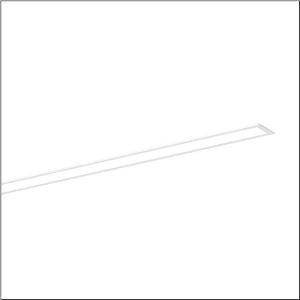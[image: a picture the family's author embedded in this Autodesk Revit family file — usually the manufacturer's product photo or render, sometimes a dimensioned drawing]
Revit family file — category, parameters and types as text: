
# Revit family: silica_r__21_51mx10db42wb_30ee
name_source: partatom
category: Lighting Fixtures
units: mm (PartAtom-declared; Revit-internal decimal feet)

## family parameters
Cut with Voids When Loaded = No
Host = Face
Light Source = No
Part Type = Normal
Room Calculation Point = No
Round Connector Dimension = Use Diameter
Shared = No

## types (1)
- --- (1 x LED, 3000 lm, 19 W, 4000K)
    Apparent Load = 19 VA
    CIE Flux Codes = 48 79 96 100 100
    Color Rendering = 80
    Color Temperature = 4000K
    Default Elevation = 1800 mm
    Description = Silica® 21, office luminaire, primary optical cover: cover, of PMMA, opal, light emission: direct distribution, primary light characteristic: symmetric, installation type: recessed, LED, rated luminous flux: 3.000lm, luminous efficacy: 158lm/W, light colour: 840, colour temperature: 4000K, with terminal, 3+2-pole, max. 2.5mm², mains connection: 220..240V, AC, 50/60Hz, rated input power: 19W, luminaire housing, of aluminium, traffic white (RAL 9016), length: 1.528mm, width: 79mm, height: 53mm, protection rating (complete): IP20, insulation class (complete): insulation class I (protective earthing), certification: CE, permissible operating ambient temperature: 0..+35°C, standard: EN 50419, packaging unit: 1 piece
    Height = 0 mm  [stored 0 ft]
    Lamp = 1 x LED
    Lamp Light Flux = 3000 lm
    Lamp Power = 19 W
    Lamp count = 1
    Length = 1527 mm
    Luminous efficacy = 158 lm/W
    Manufacturer = Siteco
    ModVariant = No
    Model = 51MX10DB42WB
    Mounting Place = Ceiling
    Mounting Type = Recessed
    Number of Poles = 1
    OnlyDefault = Yes
    Power Factor = 1
    Product Name = Silica® 21
    Product group = office luminaire | ceiling recessed
    ProductGroupID = 401
    Protection Class = Protection class I
    Protection Degree = IP 20
    RLX_Detail_Level = 1
    RLX_Emergency_Light_Flux = 0 lm
    RLX_Emergency_Type = 0
    RLX_Emergency_Type_DB = No
    RlxData = <blob elided: 20997 chars, md5=89b81c23>
    Socket = socket
    Standby Power = 0 W
    System Light Flux = 3000 lm
    System Power = 19 W
    Type Comments = factory setting: luminous flux: 100 % | dim-lin: 254 | 218 mA
    Type Image = l_1313615.jpg
    URL = http://relux.com
    VarID = @adj_065875
    Voltage = 0 V
    Weight = 0.00 kg
    Width = 79 mm

note: [stored X ft] marks values corroborated as IEEE doubles in the binary element streams (Revit-internal decimal feet)

## geometry (parser evidence)
native form markers: Blend x4, Sweep x10
no freeform markers — native parametric forms only
